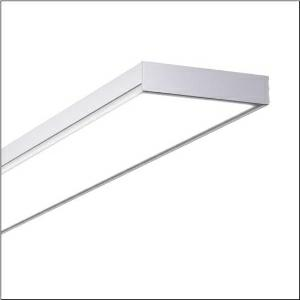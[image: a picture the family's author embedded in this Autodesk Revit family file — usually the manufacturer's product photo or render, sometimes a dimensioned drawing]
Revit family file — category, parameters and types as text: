
# Revit family: apollon_r__31_51mp25wd2441e_8772
name_source: partatom
category: Lighting Fixtures
units: mm (PartAtom-declared; Revit-internal decimal feet)

## family parameters
Cut with Voids When Loaded = No
Host = Face
Light Source = No
Part Type = Normal
Room Calculation Point = No
Round Connector Dimension = Use Diameter
Shared = No

## types (1)
- Apollon® 31 (1 x LED, 3800 lm, 28 W, 4000K)
    Apparent Load = 28 VA
    CIE Flux Codes = 61 87 97 97 100
    Color Rendering = 80
    Color Temperature = 4000K
    Default Elevation = 1800 mm
    Description = Apollon® 31, office luminaire, primary optical cover: micro prismatic cover, of PMMA, light emission: direct distribution, primary light characteristic: symmetric, installation type: surface-mounted, LED, rated luminous flux: 3.800lm, luminous efficacy: 134lm/W, light colour: 840, colour temperature: 4000K, control gear: ECG DALI, with terminal, 5-pole, mains connection: 220..240V, AC, 50/60Hz, rated input power: 28W, housing, of sheet steel, coil coated, metallic grey (RAL 9006), length: 1.245mm, width: 200mm, height: 44mm, protection rating (complete): IP20, insulation class (complete): insulation class II (safety insulation), certification: CE, impact resistance: IK02, permissible operating ambient temperature: -20..+40°C, standard: EN 60598-2-22, packaging unit: 1 piece
    Height = 44 mm
    Lamp = 1 x LED
    Lamp Light Flux = 3800 lm
    Lamp Power = 28 W
    Lamp count = 1
    Length = 1245 mm
    Luminous efficacy = 136 lm/W
    Manufacturer = Siteco
    ModVariant = No
    Model = 51MP25WD2441E
    Mounting Place = Ceiling
    Mounting Type = Surface mounted
    Number of Poles = 1
    OnlyDefault = Yes
    Power Factor = 1
    Product Name = Apollon® 31
    Product group = office luminaire | ceiling mounted
    ProductGroupID = 302
    Protection Class = Protection class II
    Protection Degree = IP 20
    RLX_Detail_Level = 1
    RlxData = <blob elided: 24101 chars, md5=ba780f87>
    Socket = socket
    Standby Power = 0 W
    System Light Flux = 3800 lm
    System Power = 28 W
    Type Comments = Product without accessories
    Type Image = l_1007091.jpg
    URL = http://relux.com
    VarID = ---
    Voltage = 0 V
    Weight = 0.00 kg
    Width = 200 mm  [stored 0.656168 ft]

note: [stored X ft] marks values corroborated as IEEE doubles in the binary element streams (Revit-internal decimal feet)

## geometry (parser evidence)
native form markers: Blend x4, Sweep x9
no freeform markers — native parametric forms only
